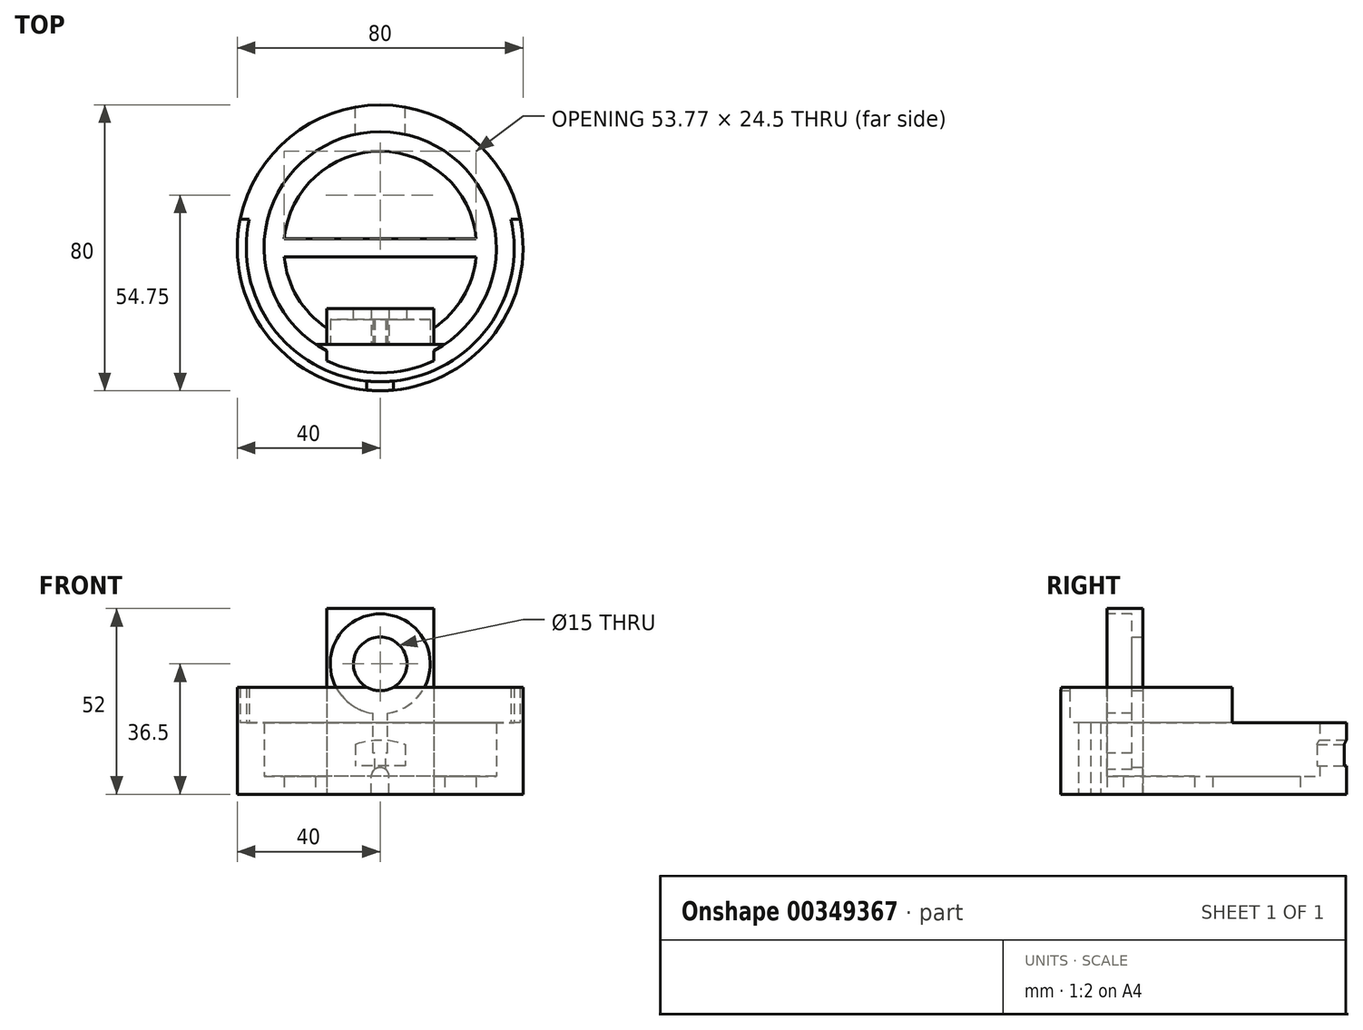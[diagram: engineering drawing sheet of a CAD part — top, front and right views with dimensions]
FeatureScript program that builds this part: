
annotation { "Feature Type Name" : "Feature", "Feature Type Description" : "" }
export const myFeature = defineFeature(function(context is Context, id is Id, definition is map)
    precondition{}
    {
        {
            assignVariable(context, id + "F0", {"name" : "h_shell", "anyValue" : 20});
        }
        {
            assignVariable(context, id + "F1", {"name" : "h_wall", "anyValue" : getVariable(context, 'h_shell') + 10});
        }
        {
            var Q0;
            Q0=qCreatedBy(makeId("Top.planeOp"),FACE);
            var sketch = newSketch(context, id + "F2", { "sketchPlane" : qUnion([Q0])});
            skCircle(sketch, "E0", {"center": v(0, 0) * mm, "radius": 35 * mm});
            skLineSegment(sketch, "E1", {"start": v(0, 0) * mm, "end": v(0, -35) * mm, "construction": true});
            skLineSegment(sketch, "E2.bottom", {"start": v(-15, -17) * mm, "end": v(15, -17) * mm});
            skLineSegment(sketch, "E2.top", {"start": v(-15, -27) * mm, "end": v(15, -27) * mm});
            skLineSegment(sketch, "E2.left", {"start": v(-15, -17) * mm, "end": v(-15, -27) * mm});
            skLineSegment(sketch, "E2.right", {"start": v(15, -17) * mm, "end": v(15, -27) * mm});
            skPoint(sketch, "E3", {"position": v(0, -17) * mm});
            skPoint(sketch, "E4", {"position": v(0, -27) * mm});
            skLineSegment(sketch, "E5", {"start": v(-15, -31.62) * mm, "end": v(-15, 31.62) * mm, "construction": true});
            skLineSegment(sketch, "E6", {"start": v(15, -31.62) * mm, "end": v(15, 31.62) * mm, "construction": true});
            skCircle(sketch, "E7", {"center": v(0, 0) * mm, "radius": 40 * mm});
            skCircle(sketch, "E8", {"center": v(0, 0) * mm, "radius": 32.5 * mm});
            skLineSegment(sketch, "E9", {"start": v(-15, -27) * mm, "end": v(-15, -31.62) * mm});
            skLineSegment(sketch, "E10", {"start": v(15, -27) * mm, "end": v(15, -31.62) * mm});
            skCircle(sketch, "E11", {"center": v(0, 0) * mm, "radius": 27 * mm});
            skLineSegment(sketch, "E12", {"start": v(-18.1, -27) * mm, "end": v(-22.27, -27) * mm});
            skLineSegment(sketch, "E13", {"start": v(18.1, -27) * mm, "end": v(22.27, -27) * mm});
            skLineSegment(sketch, "E14", {"start": v(-18.1, -27) * mm, "end": v(-15, -27) * mm});
            skLineSegment(sketch, "E15", {"start": v(15, -27) * mm, "end": v(18.1, -27) * mm});
            skLineSegment(sketch, "E16", {"start": v(-27.7, -17) * mm, "end": v(-30.6, -17) * mm});
            skLineSegment(sketch, "E17", {"start": v(27.7, -17) * mm, "end": v(30.6, -17) * mm});
            skCircle(sketch, "E18", {"center": v(0, 0) * mm, "radius": 37.5 * mm});
            skLineSegment(sketch, "E19", {"start": v(-39.2, 8) * mm, "end": v(39.2, 8) * mm});
            skLineSegment(sketch, "E20.bottom", {"start": v(30, 2.5) * mm, "end": v(-30, 2.5) * mm});
            skLineSegment(sketch, "E20.top", {"start": v(30, -2.5) * mm, "end": v(-30, -2.5) * mm});
            skLineSegment(sketch, "E20.left", {"start": v(30, 2.5) * mm, "end": v(30, -2.5) * mm});
            skLineSegment(sketch, "E20.right", {"start": v(-30, 2.5) * mm, "end": v(-30, -2.5) * mm});
            skSolve(sketch);
        }
        {
            var Q0;
            {var subQ0=sQuery(id+"F2.wireOp",EDGE,"E19");var subQ1=sQuery(id+"F2.wireOp",EDGE,"E7");var subQ2=makeQuery(id+"F2.imprint","INTERSECT",VERTEX,{"disambiguationData":[OD(0.0)],"derivedFrom":[subQ1,subQ0]});Q0=makeQuery(id+"F2.imprint","IMPRINT",FACE,{"disambiguationData":[TD([[makeQuery(id+"F2.imprint","IMPRINT",EDGE,{"disambiguationData":[TD([[subQ2,1.0]])],"derivedFrom":subQ1}),1.0]])]});}
            var Q1;
            {var subQ0=sQuery(id+"F2.wireOp",EDGE,"E19");var subQ1=sQuery(id+"F2.wireOp",EDGE,"E7");var subQ2=makeQuery(id+"F2.imprint","INTERSECT",VERTEX,{"disambiguationData":[OD(0.0)],"derivedFrom":[subQ1,subQ0]});Q1=makeQuery(id+"F2.imprint","IMPRINT",FACE,{"disambiguationData":[TD([[makeQuery(id+"F2.imprint","IMPRINT",EDGE,{"disambiguationData":[TD([[subQ2,-1.0]])],"derivedFrom":subQ1}),1.0]])]});}
            var Q2;
            {var subQ0=sQuery(id+"F2.wireOp",EDGE,"E19");var subQ1=sQuery(id+"F2.wireOp",EDGE,"E0");var subQ2=makeQuery(id+"F2.imprint","INTERSECT",VERTEX,{"disambiguationData":[OD(0.0)],"derivedFrom":[subQ1,subQ0]});Q2=makeQuery(id+"F2.imprint","IMPRINT",FACE,{"disambiguationData":[TD([[makeQuery(id+"F2.imprint","IMPRINT",EDGE,{"disambiguationData":[TD([[subQ2,1.0]])],"derivedFrom":subQ1}),-1.0]])]});}
            var Q3;
            {var subQ0=sQuery(id+"F2.wireOp",EDGE,"E0");var subQ4=makeQuery(id+"F2.imprint","INTERSECT",VERTEX,{"derivedFrom":[subQ0,sQuery(id+"F2.wireOp",EDGE,"E16")]});Q3=makeQuery(id+"F2.imprint","IMPRINT",FACE,{"disambiguationData":[TD([[makeQuery(id+"F2.imprint","IMPRINT",EDGE,{"disambiguationData":[TD([[subQ4,1.0]])],"derivedFrom":subQ0}),-1.0]])]});}
            var Q4;
            {var subQ0=sQuery(id+"F2.wireOp",EDGE,"E16");Q4=makeQuery(id+"F2.imprint","IMPRINT",FACE,{"disambiguationData":[TD([[makeQuery(id+"F2.imprint","IMPRINT",EDGE,{"derivedFrom":subQ0}),-1.0]])]});}
            var Q5;
            {var subQ0=sQuery(id+"F2.wireOp",EDGE,"E19");var subQ1=sQuery(id+"F2.wireOp",EDGE,"E0");var subQ2=makeQuery(id+"F2.imprint","INTERSECT",VERTEX,{"disambiguationData":[OD(0.0)],"derivedFrom":[subQ1,subQ0]});Q5=makeQuery(id+"F2.imprint","IMPRINT",FACE,{"disambiguationData":[TD([[makeQuery(id+"F2.imprint","IMPRINT",EDGE,{"disambiguationData":[TD([[subQ2,1.0]])],"derivedFrom":subQ1}),1.0]])]});}
            var Q6;
            {var subQ0=sQuery(id+"F2.wireOp",EDGE,"E17");Q6=makeQuery(id+"F2.imprint","IMPRINT",FACE,{"disambiguationData":[TD([[makeQuery(id+"F2.imprint","IMPRINT",EDGE,{"derivedFrom":subQ0}),1.0]])]});}
            var Q7;
            {var subQ0=sQuery(id+"F2.wireOp",EDGE,"E12");Q7=makeQuery(id+"F2.imprint","IMPRINT",FACE,{"disambiguationData":[TD([[makeQuery(id+"F2.imprint","IMPRINT",EDGE,{"derivedFrom":subQ0}),-1.0]])]});}
            var Q8;
            {var subQ0=sQuery(id+"F2.wireOp",EDGE,"E13");Q8=makeQuery(id+"F2.imprint","IMPRINT",FACE,{"disambiguationData":[TD([[makeQuery(id+"F2.imprint","IMPRINT",EDGE,{"derivedFrom":subQ0}),1.0]])]});}
            var Q9;
            {var subQ3=sQuery(id+"F2.wireOp",EDGE,"E12");Q9=makeQuery(id+"F2.imprint","IMPRINT",FACE,{"disambiguationData":[TD([[makeQuery(id+"F2.imprint","IMPRINT",EDGE,{"derivedFrom":subQ3}),1.0]])]});}
            var Q10;
            {var subQ3=sQuery(id+"F2.wireOp",EDGE,"E13");Q10=makeQuery(id+"F2.imprint","IMPRINT",FACE,{"disambiguationData":[TD([[makeQuery(id+"F2.imprint","IMPRINT",EDGE,{"derivedFrom":subQ3}),-1.0]])]});}
            extrude(context, id + "F3", {"entities" : qUnion([Q0, Q1, Q2, Q3, Q4, Q5, Q6, Q7, Q8, Q9, Q10]), "depth" : getVariable(context, 'h_shell') * mm});
        }
        {
            var Q0;
            {var subQ0=sQuery(id+"F2.wireOp",EDGE,"E19");var subQ1=sQuery(id+"F2.wireOp",EDGE,"E7");var subQ2=makeQuery(id+"F2.imprint","INTERSECT",VERTEX,{"disambiguationData":[OD(0.0)],"derivedFrom":[subQ1,subQ0]});Q0=makeQuery(id+"F2.imprint","IMPRINT",FACE,{"disambiguationData":[TD([[makeQuery(id+"F2.imprint","IMPRINT",EDGE,{"disambiguationData":[TD([[subQ2,1.0]])],"derivedFrom":subQ1}),1.0]])]});}
            extrude(context, id + "F4", {"entities" : qUnion([Q0]), "operationType" : NewBodyOperationType.ADD, "depth" : getVariable(context, 'h_wall') * mm});
        }
        {
            var Q0;
            {var subQ5=sQuery(id+"F2.wireOp",EDGE,"E14");Q0=makeQuery(id+"F2.imprint","IMPRINT",FACE,{"disambiguationData":[TD([[makeQuery(id+"F2.imprint","IMPRINT",EDGE,{"derivedFrom":subQ5}),1.0]])]});}
            var Q1;
            {var subQ0=sQuery(id+"F2.wireOp",EDGE,"E12");Q1=makeQuery(id+"F2.imprint","IMPRINT",FACE,{"disambiguationData":[TD([[makeQuery(id+"F2.imprint","IMPRINT",EDGE,{"derivedFrom":subQ0}),-1.0]])]});}
            var Q2;
            {var subQ0=sQuery(id+"F2.wireOp",EDGE,"E13");Q2=makeQuery(id+"F2.imprint","IMPRINT",FACE,{"disambiguationData":[TD([[makeQuery(id+"F2.imprint","IMPRINT",EDGE,{"derivedFrom":subQ0}),1.0]])]});}
            var Q3;
            {var subQ5=sQuery(id+"F2.wireOp",EDGE,"E15");Q3=makeQuery(id+"F2.imprint","IMPRINT",FACE,{"disambiguationData":[TD([[makeQuery(id+"F2.imprint","IMPRINT",EDGE,{"derivedFrom":subQ5}),1.0]])]});}
            var Q4;
            {var subQ0=sQuery(id+"F2.wireOp",EDGE,"E17");Q4=makeQuery(id+"F2.imprint","IMPRINT",FACE,{"disambiguationData":[TD([[makeQuery(id+"F2.imprint","IMPRINT",EDGE,{"derivedFrom":subQ0}),1.0]])]});}
            var Q5;
            {var subQ0=sQuery(id+"F2.wireOp",EDGE,"E19");var subQ1=sQuery(id+"F2.wireOp",EDGE,"E8");var subQ2=makeQuery(id+"F2.imprint","INTERSECT",VERTEX,{"disambiguationData":[OD(0.0)],"derivedFrom":[subQ1,subQ0]});Q5=makeQuery(id+"F2.imprint","IMPRINT",FACE,{"disambiguationData":[TD([[makeQuery(id+"F2.imprint","IMPRINT",EDGE,{"disambiguationData":[TD([[subQ2,1.0]])],"derivedFrom":subQ1}),1.0]])]});}
            var Q6;
            {var subQ0=sQuery(id+"F2.wireOp",EDGE,"E19");var subQ1=sQuery(id+"F2.wireOp",EDGE,"E0");var subQ2=makeQuery(id+"F2.imprint","INTERSECT",VERTEX,{"disambiguationData":[OD(0.0)],"derivedFrom":[subQ1,subQ0]});Q6=makeQuery(id+"F2.imprint","IMPRINT",FACE,{"disambiguationData":[TD([[makeQuery(id+"F2.imprint","IMPRINT",EDGE,{"disambiguationData":[TD([[subQ2,1.0]])],"derivedFrom":subQ1}),1.0]])]});}
            var Q7;
            {var subQ5=sQuery(id+"F2.wireOp",EDGE,"E20.right");Q7=makeQuery(id+"F2.imprint","IMPRINT",FACE,{"disambiguationData":[TD([[makeQuery(id+"F2.imprint","IMPRINT",EDGE,{"derivedFrom":subQ5}),1.0]])]});}
            var Q8;
            {var subQ5=sQuery(id+"F2.wireOp",EDGE,"E20.left");Q8=makeQuery(id+"F2.imprint","IMPRINT",FACE,{"disambiguationData":[TD([[makeQuery(id+"F2.imprint","IMPRINT",EDGE,{"derivedFrom":subQ5}),-1.0]])]});}
            var Q9;
            {var subQ0=sQuery(id+"F2.wireOp",EDGE,"E20.bottom");var subQ1=sQuery(id+"F2.wireOp",EDGE,"E11");var subQ2=makeQuery(id+"F2.imprint","INTERSECT",VERTEX,{"disambiguationData":[OD(1.0)],"derivedFrom":[subQ1,subQ0]});Q9=makeQuery(id+"F2.imprint","IMPRINT",FACE,{"disambiguationData":[TD([[makeQuery(id+"F2.imprint","IMPRINT",EDGE,{"disambiguationData":[TD([[subQ2,-1.0]])],"derivedFrom":subQ1}),1.0]])]});}
            extrude(context, id + "F5", {"entities" : qUnion([Q0, Q1, Q2, Q3, Q4, Q5, Q6, Q7, Q8, Q9]), "operationType" : NewBodyOperationType.ADD, "depth" : 5 * mm});
        }
        {
            var Q0;
            {var subQ5=sQuery(id+"F2.wireOp",EDGE,"E2.bottom");Q0=makeQuery(id+"F2.imprint","IMPRINT",FACE,{"disambiguationData":[TD([[makeQuery(id+"F2.imprint","IMPRINT",EDGE,{"derivedFrom":subQ5}),-1.0]])]});}
            var Q1;
            {var subQ1=sQuery(id+"F2.wireOp",EDGE,"E2.top");var subQ3=sQuery(id+"F2.wireOp",EDGE,"E11");var subQ4=makeQuery(id+"F2.imprint","INTERSECT",VERTEX,{"derivedFrom":[subQ1,subQ3]});Q1=makeQuery(id+"F2.imprint","IMPRINT",FACE,{"disambiguationData":[TD([[makeQuery(id+"F2.imprint","IMPRINT",EDGE,{"disambiguationData":[TD([[subQ4,1.0]])],"derivedFrom":subQ3}),-1.0]])]});}
            var Q2;
            {var subQ1=sQuery(id+"F2.wireOp",EDGE,"E2.top");var subQ3=sQuery(id+"F2.wireOp",EDGE,"E11");var subQ4=makeQuery(id+"F2.imprint","INTERSECT",VERTEX,{"derivedFrom":[subQ1,subQ3]});Q2=makeQuery(id+"F2.imprint","IMPRINT",FACE,{"disambiguationData":[TD([[makeQuery(id+"F2.imprint","IMPRINT",EDGE,{"disambiguationData":[TD([[subQ4,-1.0]])],"derivedFrom":subQ3}),-1.0]])]});}
            extrude(context, id + "F6", {"entities" : qUnion([Q0, Q1, Q2]), "operationType" : NewBodyOperationType.ADD, "depth" : 52 * mm});
        }
        {
            var Q0;
            Q0=makeQuery(id+"F6.boolean.opBoolean","MERGE",FACE,{"derivedFrom":[makeQuery(id+"F5.opExtrude","SWEPT_FACE",FACE,{"disambiguationData":[OSD([sQuery(id+"F2.wireOp",EDGE,"E12"),sQuery(id+"F2.wireOp",EDGE,"E14")])]}),makeQuery(id+"F5.opExtrude","SWEPT_FACE",FACE,{"disambiguationData":[OSD([sQuery(id+"F2.wireOp",EDGE,"E13"),sQuery(id+"F2.wireOp",EDGE,"E15")])]}),makeQuery(id+"F6.opExtrude","SWEPT_FACE",FACE,{"disambiguationData":[OSD([sQuery(id+"F2.wireOp",EDGE,"E2.top")])]})]});
            var sketch = newSketch(context, id + "F7", { "sketchPlane" : qUnion([Q0])});
            skLineSegment(sketch, "E21.0", {"start": v(-27, 0) * mm, "end": v(27, 0) * mm, "construction": true});
            skLineSegment(sketch, "E22.bottom", {"start": v(2.5, 0) * mm, "end": v(-2.5, 0) * mm});
            skLineSegment(sketch, "E22.top", {"start": v(2.5, 5) * mm, "end": v(-2.5, 5) * mm});
            skLineSegment(sketch, "E22.left", {"start": v(2.5, 0) * mm, "end": v(2.5, 5) * mm});
            skLineSegment(sketch, "E22.right", {"start": v(-2.5, 0) * mm, "end": v(-2.5, 5) * mm});
            skPoint(sketch, "E23", {"position": v(0, 5) * mm});
            skLineSegment(sketch, "E24", {"start": v(0, 0) * mm, "end": v(0, 52) * mm, "construction": true});
            skCircle(sketch, "E25", {"center": v(0, 5) * mm, "radius": 2.5 * mm});
            skPoint(sketch, "E26", {"position": v(0, 7.5) * mm});
            skLineSegment(sketch, "E27", {"start": v(-10.56, 7.5) * mm, "end": v(10.96, 7.5) * mm, "construction": true});
            skLineSegment(sketch, "E28.bottom", {"start": v(1.5, 7.5) * mm, "end": v(-1.5, 7.5) * mm});
            skLineSegment(sketch, "E28.top", {"start": v(1.5, 11.5) * mm, "end": v(-1.5, 11.5) * mm});
            skLineSegment(sketch, "E28.left", {"start": v(1.5, 7.5) * mm, "end": v(1.5, 11.5) * mm});
            skLineSegment(sketch, "E28.right", {"start": v(-1.5, 7.5) * mm, "end": v(-1.5, 11.5) * mm});
            skPoint(sketch, "E29", {"position": v(0, 11.5) * mm});
            skLineSegment(sketch, "E30.bottom", {"start": v(2, 11.5) * mm, "end": v(-2, 11.5) * mm});
            skLineSegment(sketch, "E30.top", {"start": v(2, 22.5) * mm, "end": v(-2, 22.5) * mm});
            skLineSegment(sketch, "E30.left", {"start": v(2, 11.5) * mm, "end": v(2, 22.5) * mm});
            skLineSegment(sketch, "E30.right", {"start": v(-2, 11.5) * mm, "end": v(-2, 22.5) * mm});
            skPoint(sketch, "E31", {"position": v(0, 22.5) * mm});
            skCircle(sketch, "E32", {"center": v(0, 36.5) * mm, "radius": 14 * mm});
            skLineSegment(sketch, "E33", {"start": v(-2, 22.5) * mm, "end": v(-2, 22.64) * mm});
            skLineSegment(sketch, "E34", {"start": v(2, 22.5) * mm, "end": v(2, 22.64) * mm});
            skLineSegment(sketch, "E35", {"start": v(-1.5, 7.5) * mm, "end": v(-1.5, 7) * mm});
            skLineSegment(sketch, "E36", {"start": v(1.5, 7.5) * mm, "end": v(1.5, 7) * mm});
            skLineSegment(sketch, "E37", {"start": v(-15, 22.5) * mm, "end": v(15, 22.5) * mm, "construction": true});
            skLineSegment(sketch, "E38", {"start": v(-15, 17.5) * mm, "end": v(15, 17.5) * mm, "construction": true});
            skLineSegment(sketch, "E39", {"start": v(-15, 20) * mm, "end": v(15, 20) * mm, "construction": true});
            skSolve(sketch);
        }
        {
            var Q0;
            {var subQ3=sQuery(id+"F7.wireOp",EDGE,"E22.top");Q0=makeQuery(id+"F7.imprint","IMPRINT",FACE,{"disambiguationData":[TD([[makeQuery(id+"F7.imprint","IMPRINT",EDGE,{"derivedFrom":subQ3}),-1.0]])]});}
            var Q1;
            {var subQ0=sQuery(id+"F7.wireOp",EDGE,"E22.top");Q1=makeQuery(id+"F7.imprint","IMPRINT",FACE,{"disambiguationData":[TD([[makeQuery(id+"F7.imprint","IMPRINT",EDGE,{"derivedFrom":subQ0}),1.0]])]});}
            var Q2;
            Q2=makeQuery(id+"F7.imprint","IMPRINT",FACE,{"disambiguationData":[TD([[makeQuery(id+"F7.imprint","IMPRINT",EDGE,{"derivedFrom":sQuery(id+"F7.wireOp",EDGE,"E22.bottom")}),1.0]])]});
            extrude(context, id + "F8", {"entities" : qUnion([Q0, Q1, Q2]), "operationType" : NewBodyOperationType.REMOVE, "oppositeDirection" : true, "depth" : 10 * mm});
        }
        {
            var Q0;
            {var subQ1=sQuery(id+"F7.wireOp",EDGE,"E28.left");Q0=makeQuery(id+"F7.imprint","IMPRINT",FACE,{"disambiguationData":[TD([[makeQuery(id+"F7.imprint","IMPRINT",EDGE,{"derivedFrom":subQ1}),1.0]])]});}
            var Q1;
            {var subQ0=sQuery(id+"F7.wireOp",EDGE,"E30.left");Q1=makeQuery(id+"F7.imprint","IMPRINT",FACE,{"disambiguationData":[TD([[makeQuery(id+"F7.imprint","IMPRINT",EDGE,{"derivedFrom":subQ0}),1.0]])]});}
            var Q2;
            {var subQ0=sQuery(id+"F7.wireOp",EDGE,"E35");Q2=makeQuery(id+"F7.imprint","IMPRINT",FACE,{"disambiguationData":[TD([[makeQuery(id+"F7.imprint","IMPRINT",EDGE,{"derivedFrom":subQ0}),1.0]])]});}
            var Q3;
            {var subQ0=sQuery(id+"F7.wireOp",EDGE,"E36");Q3=makeQuery(id+"F7.imprint","IMPRINT",FACE,{"disambiguationData":[TD([[makeQuery(id+"F7.imprint","IMPRINT",EDGE,{"derivedFrom":subQ0}),-1.0]])]});}
            var Q4;
            {var subQ0=sQuery(id+"F7.wireOp",EDGE,"E32");var subQ1=makeQuery(id+"F7.imprint","INTERSECT",VERTEX,{"derivedFrom":[subQ0,sQuery(id+"F7.wireOp",EDGE,"E33")]});Q4=makeQuery(id+"F7.imprint","IMPRINT",FACE,{"disambiguationData":[TD([[makeQuery(id+"F7.imprint","IMPRINT",EDGE,{"disambiguationData":[TD([[subQ1,-1.0]])],"derivedFrom":subQ0}),1.0]])]});}
            var Q5;
            {var subQ0=sQuery(id+"F7.wireOp",EDGE,"E33");Q5=makeQuery(id+"F7.imprint","IMPRINT",FACE,{"disambiguationData":[TD([[makeQuery(id+"F7.imprint","IMPRINT",EDGE,{"derivedFrom":subQ0}),-1.0]])]});}
            var Q6;
            {var subQ0=sQuery(id+"F7.wireOp",EDGE,"E34");Q6=makeQuery(id+"F7.imprint","IMPRINT",FACE,{"disambiguationData":[TD([[makeQuery(id+"F7.imprint","IMPRINT",EDGE,{"derivedFrom":subQ0}),1.0]])]});}
            extrude(context, id + "F9", {"entities" : qUnion([Q0, Q1, Q2, Q3, Q4, Q5, Q6]), "operationType" : NewBodyOperationType.REMOVE, "oppositeDirection" : true, "depth" : 7 * mm});
        }
        {
            var Q0;
            Q0=qCreatedBy(makeId("Front.planeOp"),FACE);
            cPlane(context, id + "F10", {"entities" : qUnion([Q0]), "cplaneType" : CPlaneType.OFFSET, "offset" : 40 * mm, "oppositeDirection" : true, "width" : 150 * mm, "height" : 150 * mm});
        }
        {
            var Q0;
            Q0=qCreatedBy(id+"F10.planeOp",FACE);
            var sketch = newSketch(context, id + "F11", { "sketchPlane" : qUnion([Q0])});
            skLineSegment(sketch, "E40.0", {"start": v(0, 0) * mm, "end": v(0, 52) * mm, "construction": true});
            skLineSegment(sketch, "E41.bottom", {"start": v(-7, 8) * mm, "end": v(7, 8) * mm});
            skLineSegment(sketch, "E41.top", {"start": v(-7, 14) * mm, "end": v(7, 14) * mm});
            skLineSegment(sketch, "E41.left", {"start": v(-7, 8) * mm, "end": v(-7, 14) * mm});
            skLineSegment(sketch, "E41.right", {"start": v(7, 8) * mm, "end": v(7, 14) * mm});
            skPoint(sketch, "E41.middle", {"position": v(0, 11) * mm});
            skArc(sketch, "E42", {"start": v(7, 14) * mm, "mid": v(0, 15.27) * mm, "end": v(-7, 14) * mm});
            skSolve(sketch);
        }
        {
            var Q0;
            Q0 = qSketchRegion(id + "F11", true);
            extrude(context, id + "F12", {"entities" : qUnion([Q0]), "operationType" : NewBodyOperationType.REMOVE, "depth" : 20 * mm});
        }
        {
            var Q0;
            Q0=makeQuery(id+"F6.opExtrude","SWEPT_FACE",FACE,{"disambiguationData":[OSD([sQuery(id+"F2.wireOp",EDGE,"E2.bottom")])]});
            var sketch = newSketch(context, id + "F13", { "sketchPlane" : qUnion([Q0])});
            skCircle(sketch, "E43.0", {"center": v(0, 36.5) * mm, "radius": 14 * mm, "construction": true});
            skCircle(sketch, "E44", {"center": v(0, 36.5) * mm, "radius": 7.5 * mm});
            skSolve(sketch);
        }
        {
            var Q0;
            Q0=makeQuery(id+"F13.imprint","IMPRINT",FACE,{"disambiguationData":[TD([[makeQuery(id+"F13.imprint","IMPRINT",EDGE,{"derivedFrom":sQuery(id+"F13.wireOp",EDGE,"E44")}),1.0]])]});
            extrude(context, id + "F14", {"entities" : qUnion([Q0]), "operationType" : NewBodyOperationType.REMOVE, "oppositeDirection" : true, "depth" : 25 * mm});
        }
    });
